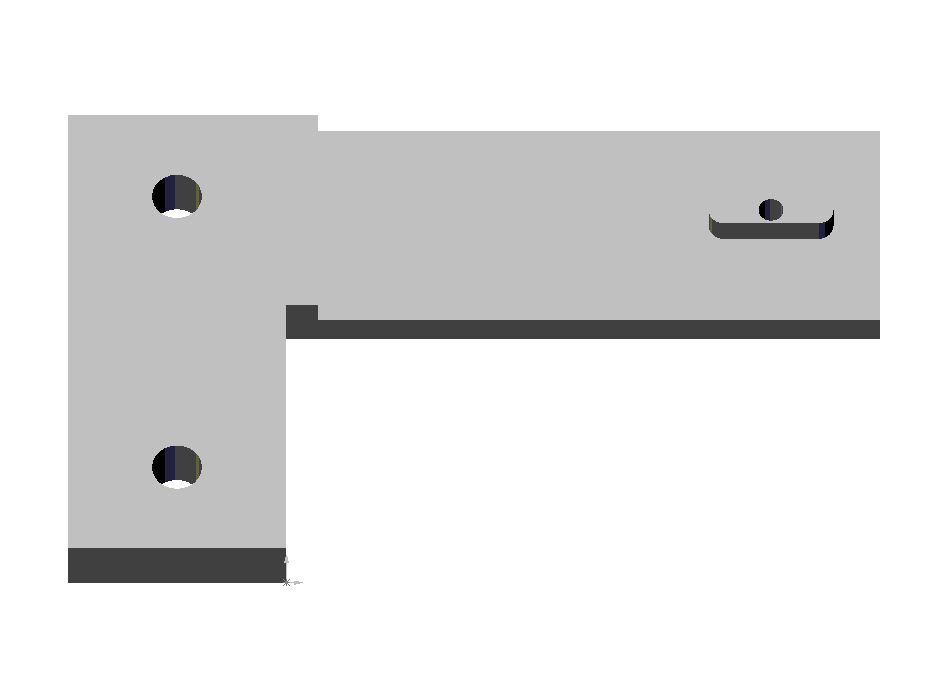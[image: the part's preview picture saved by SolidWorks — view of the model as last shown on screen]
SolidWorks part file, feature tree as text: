
SOLIDWORKS PART (.sldprt)
format: sldprt  version: not decoded by parser v0  size: 147,456 bytes
history: native  units: mm
features: sketch x4, plane x3, cut_extrude x3, extrude x1 (+5 scaffold rows collapsed)
feature tree (16):
  scaffold x5  (default folders/planes/origin — collapsed)
  plane  "Plane1"
  plane  "Plane2"
  plane  "Plane3"
  sketch  "Sketch1"  dims[D1=35.0mm D2=80.0mm D3=130.0mm D4=35.0mm]
  extrude  "Base-Extrude"  Depth=11mm
  sketch  "Sketch2"  dims[D3=8.0mm D1=17.5mm D2=40.0mm D4=25.0mm]
  cut_extrude  "Cut-Extrude1"  [1 undecoded]
  sketch  "Sketch3"  dims[c1.D6=5.0mm c1.D7=5.0mm c1.D1=40.0mm c1.D2=90.0mm c1.D3=17.5mm c1.D4=5.0mm c2.D4=90.0deg c3.D4=15.0mm c3.D5=5.0mm c3.D8=105.0mm]
  cut_extrude  "Cut-Extrude2"  Depth=5mm
  sketch  "Sketch4"  dims[D1=4.0mm D2=7.5mm D3=2.5mm]
  cut_extrude  "Cut-Extrude3"  [1 undecoded]
decode coverage: 6 of 8 modeling features carry decoded parameters
note: 2 parameter values undecoded
note: suppression state not decoded; provenance and decode notes live in map.json
